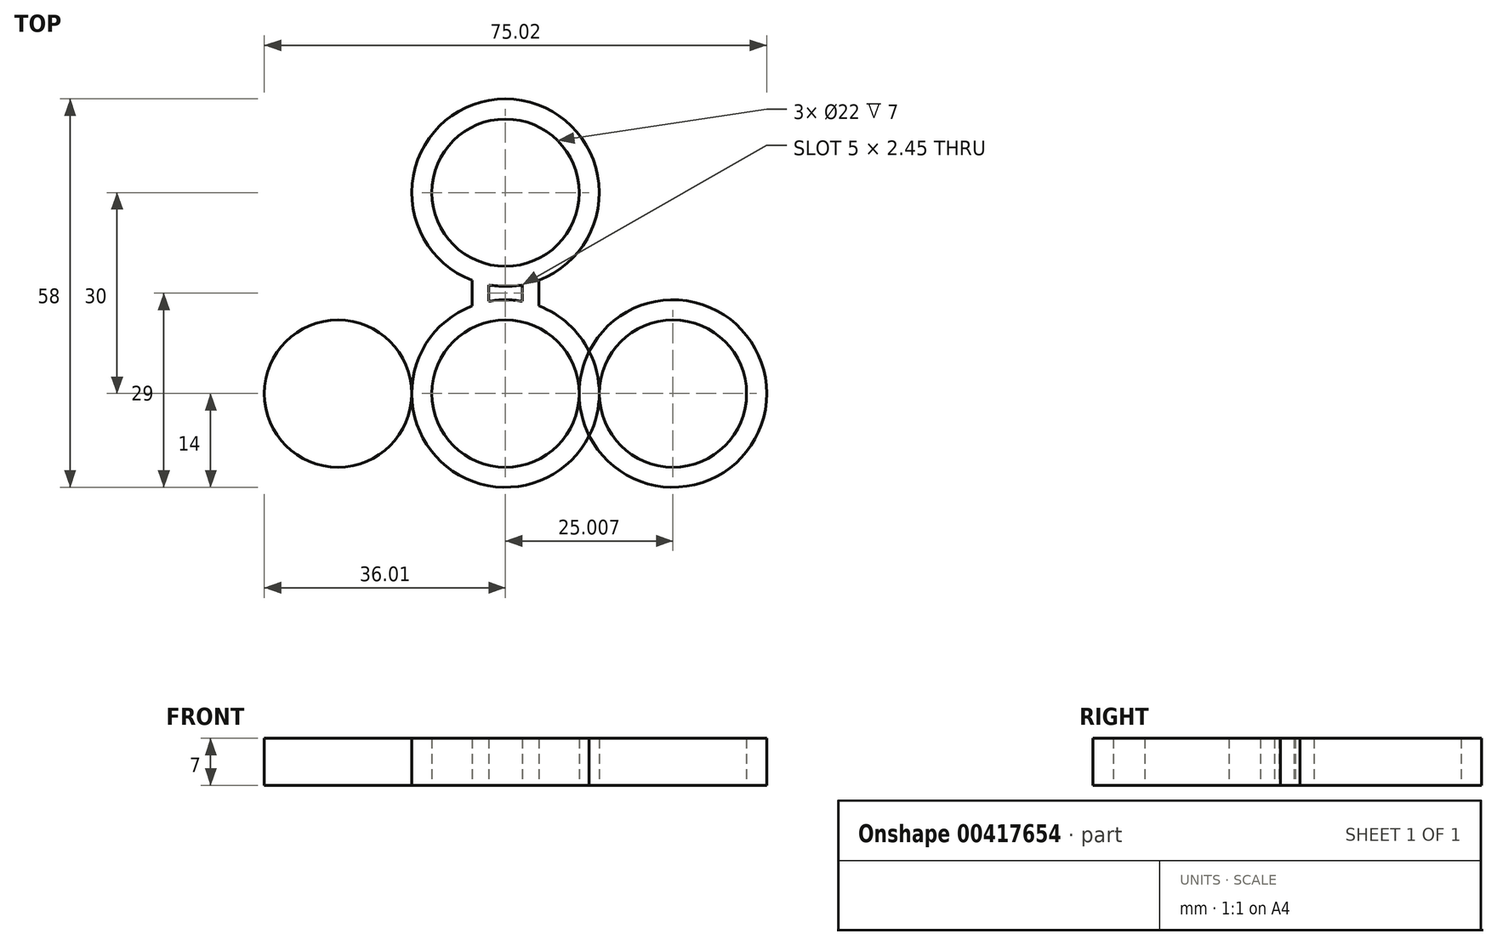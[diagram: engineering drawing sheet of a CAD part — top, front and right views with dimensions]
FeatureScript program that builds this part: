
annotation { "Feature Type Name" : "Feature", "Feature Type Description" : "" }
export const myFeature = defineFeature(function(context is Context, id is Id, definition is map)
    precondition{}
    {
        {
            var Q0;
            Q0=qCreatedBy(makeId("Top.planeOp"),FACE);
            var sketch = newSketch(context, id + "F0", { "sketchPlane" : qUnion([Q0])});
            skCircle(sketch, "E0", {"center": v(0, 0) * mm, "radius": 11 * mm});
            skCircle(sketch, "E1", {"center": v(0, 30) * mm, "radius": 11 * mm});
            skPoint(sketch, "E2", {"position": v(0, 44) * mm});
            skPoint(sketch, "E3", {"position": v(2.5, 16.92) * mm});
            skPoint(sketch, "E4", {"position": v(-2.5, 16.92) * mm});
            skPoint(sketch, "E5", {"position": v(-2.5, 13.08) * mm});
            skPoint(sketch, "E6", {"position": v(2.5, 13.08) * mm});
            skLineSegment(sketch, "E7", {"start": v(-2.5, 16.92) * mm, "end": v(-2.5, 13.08) * mm});
            skLineSegment(sketch, "E8", {"start": v(-5, 16.92) * mm, "end": v(-5, 13.08) * mm});
            skLineSegment(sketch, "E9", {"start": v(2.5, 16.92) * mm, "end": v(2.5, 13.08) * mm});
            skLineSegment(sketch, "E10", {"start": v(5, 16.92) * mm, "end": v(5, 13.08) * mm});
            skArc(sketch, "E11", {"start": v(5, 16.92) * mm, "mid": v(0, 44) * mm, "end": v(-5, 16.92) * mm});
            skArc(sketch, "E12", {"start": v(-2.5, 16.23) * mm, "mid": v(0, 16) * mm, "end": v(2.5, 16.23) * mm});
            skArc(sketch, "E13", {"start": v(-5, 13.08) * mm, "mid": v(0, -14) * mm, "end": v(5, 13.08) * mm});
            skArc(sketch, "E14", {"start": v(5, 13.08) * mm, "mid": v(3.77, 13.48) * mm, "end": v(2.5, 13.77) * mm});
            skArc(sketch, "E15", {"start": v(2.5, 13.77) * mm, "mid": v(0, 14) * mm, "end": v(-2.5, 13.77) * mm});
            skArc(sketch, "E16", {"start": v(-2.5, 13.77) * mm, "mid": v(-3.77, 13.48) * mm, "end": v(-5, 13.08) * mm});
            skCircle(sketch, "E17", {"center": v(25, 0) * mm, "radius": 11 * mm});
            skCircle(sketch, "E18.0", {"center": v(25, 0) * mm, "radius": 14 * mm});
            skArc(sketch, "E19.MirrorCS", {"start": v(5, -16.92) * mm, "mid": v(0, -44) * mm, "end": v(-5, -16.92) * mm});
            skCircle(sketch, "E20.MirrorC", {"center": v(0, -30) * mm, "radius": 11 * mm});
            skArc(sketch, "E21.MirrorCS", {"start": v(-2.5, -16.23) * mm, "mid": v(0, -16) * mm, "end": v(2.5, -16.23) * mm});
            skLineSegment(sketch, "E22.MirrorCS", {"start": v(2.5, -16.92) * mm, "end": v(2.5, -13.08) * mm});
            skLineSegment(sketch, "E23.MirrorCS", {"start": v(5, -16.92) * mm, "end": v(5, -13.08) * mm});
            skLineSegment(sketch, "E24.MirrorCS", {"start": v(-5, -16.92) * mm, "end": v(-5, -13.08) * mm});
            skLineSegment(sketch, "E25.MirrorCS", {"start": v(-2.5, -16.92) * mm, "end": v(-2.5, -13.08) * mm});
            skCircle(sketch, "E26.MirrorC", {"center": v(-25, 0) * mm, "radius": 11 * mm});
            skCircle(sketch, "E27.MirrorC", {"center": v(-25, 0) * mm, "radius": 14 * mm});
            skSolve(sketch);
        }
        {
            var Q0;
            Q0=makeQuery(id+"F0.imprint","IMPRINT",FACE,{"disambiguationData":[TD([[makeQuery(id+"F0.imprint","IMPRINT",EDGE,{"derivedFrom":sQuery(id+"F0.wireOp",EDGE,"E1")}),-1.0]])]});
            var Q1;
            Q1=makeQuery(id+"F0.imprint","IMPRINT",FACE,{"disambiguationData":[TD([[makeQuery(id+"F0.imprint","IMPRINT",EDGE,{"derivedFrom":sQuery(id+"F0.wireOp",EDGE,"E0")}),-1.0]])]});
            var Q2;
            Q2=makeQuery(id+"F0.imprint","IMPRINT",FACE,{"disambiguationData":[TD([[makeQuery(id+"F0.imprint","IMPRINT",EDGE,{"derivedFrom":sQuery(id+"F0.wireOp",EDGE,"E26.MirrorC")}),1.0]])]});
            var Q3;
            {var subQ0=sQuery(id+"F0.wireOp",EDGE,"E27.MirrorC");var subQ1=sQuery(id+"F0.wireOp",EDGE,"E13");var subQ2=makeQuery(id+"F0.imprint","INTERSECT",VERTEX,{"disambiguationData":[OD(0.0)],"derivedFrom":[subQ1,subQ0]});Q3=makeQuery(id+"F0.imprint","IMPRINT",FACE,{"disambiguationData":[TD([[makeQuery(id+"F0.imprint","IMPRINT",EDGE,{"disambiguationData":[TD([[subQ2,-1.0]])],"derivedFrom":subQ1}),1.0]])]});}
            var Q4;
            {var subQ0=sQuery(id+"F0.wireOp",EDGE,"E18.0");var subQ1=sQuery(id+"F0.wireOp",EDGE,"E13");var subQ2=makeQuery(id+"F0.imprint","INTERSECT",VERTEX,{"disambiguationData":[OD(0.0)],"derivedFrom":[subQ1,subQ0]});Q4=makeQuery(id+"F0.imprint","IMPRINT",FACE,{"disambiguationData":[TD([[makeQuery(id+"F0.imprint","IMPRINT",EDGE,{"disambiguationData":[TD([[subQ2,-1.0]])],"derivedFrom":subQ1}),1.0]])]});}
            var Q5;
            Q5=makeQuery(id+"F0.imprint","IMPRINT",FACE,{"disambiguationData":[TD([[makeQuery(id+"F0.imprint","IMPRINT",EDGE,{"derivedFrom":sQuery(id+"F0.wireOp",EDGE,"E17")}),-1.0]])]});
            var Q6;
            Q6=makeQuery(id+"F0.imprint","IMPRINT",FACE,{"disambiguationData":[TD([[makeQuery(id+"F0.imprint","IMPRINT",EDGE,{"derivedFrom":sQuery(id+"F0.wireOp",EDGE,"E19.MirrorCS")}),-1.0]])]});
            extrude(context, id + "F1", {"entities" : qUnion([Q0, Q1, Q2, Q3, Q4, Q5, Q6]), "endBound" : BoundingType.SYMMETRIC, "depth" : 7 * mm});
        }
    });
